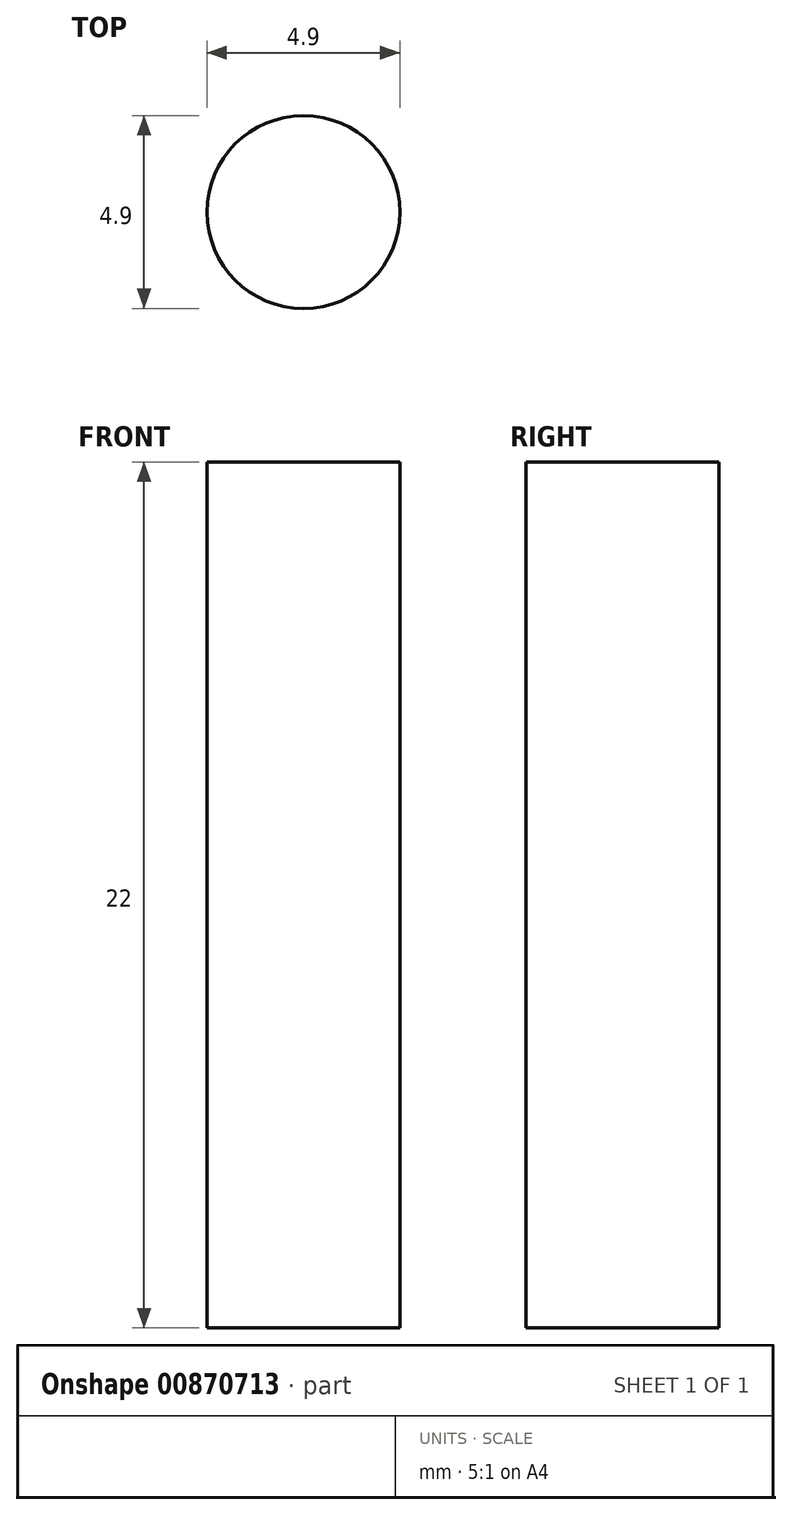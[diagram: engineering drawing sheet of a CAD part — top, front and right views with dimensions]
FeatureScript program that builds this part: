
annotation { "Feature Type Name" : "Feature", "Feature Type Description" : "" }
export const myFeature = defineFeature(function(context is Context, id is Id, definition is map)
    precondition{}
    {
        {
            var Q0;
            Q0=qCreatedBy(makeId("Top.planeOp"),FACE);
            var sketch = newSketch(context, id + "F0", { "sketchPlane" : qUnion([Q0])});
            skCircle(sketch, "E0", {"center": v(0, 0) * mm, "radius": 2.45 * mm});
            skSolve(sketch);
        }
        {
            var Q0;
            Q0=makeQuery(id+"F0.imprint","IMPRINT",FACE,{"disambiguationData":[TD([[makeQuery(id+"F0.imprint","IMPRINT",EDGE,{"derivedFrom":sQuery(id+"F0.wireOp",EDGE,"E0")}),1.0]])]});
            extrude(context, id + "F1", {"entities" : qUnion([Q0]), "depth" : 22 * mm, "offsetDistance" : 25 * mm});
        }
    });
